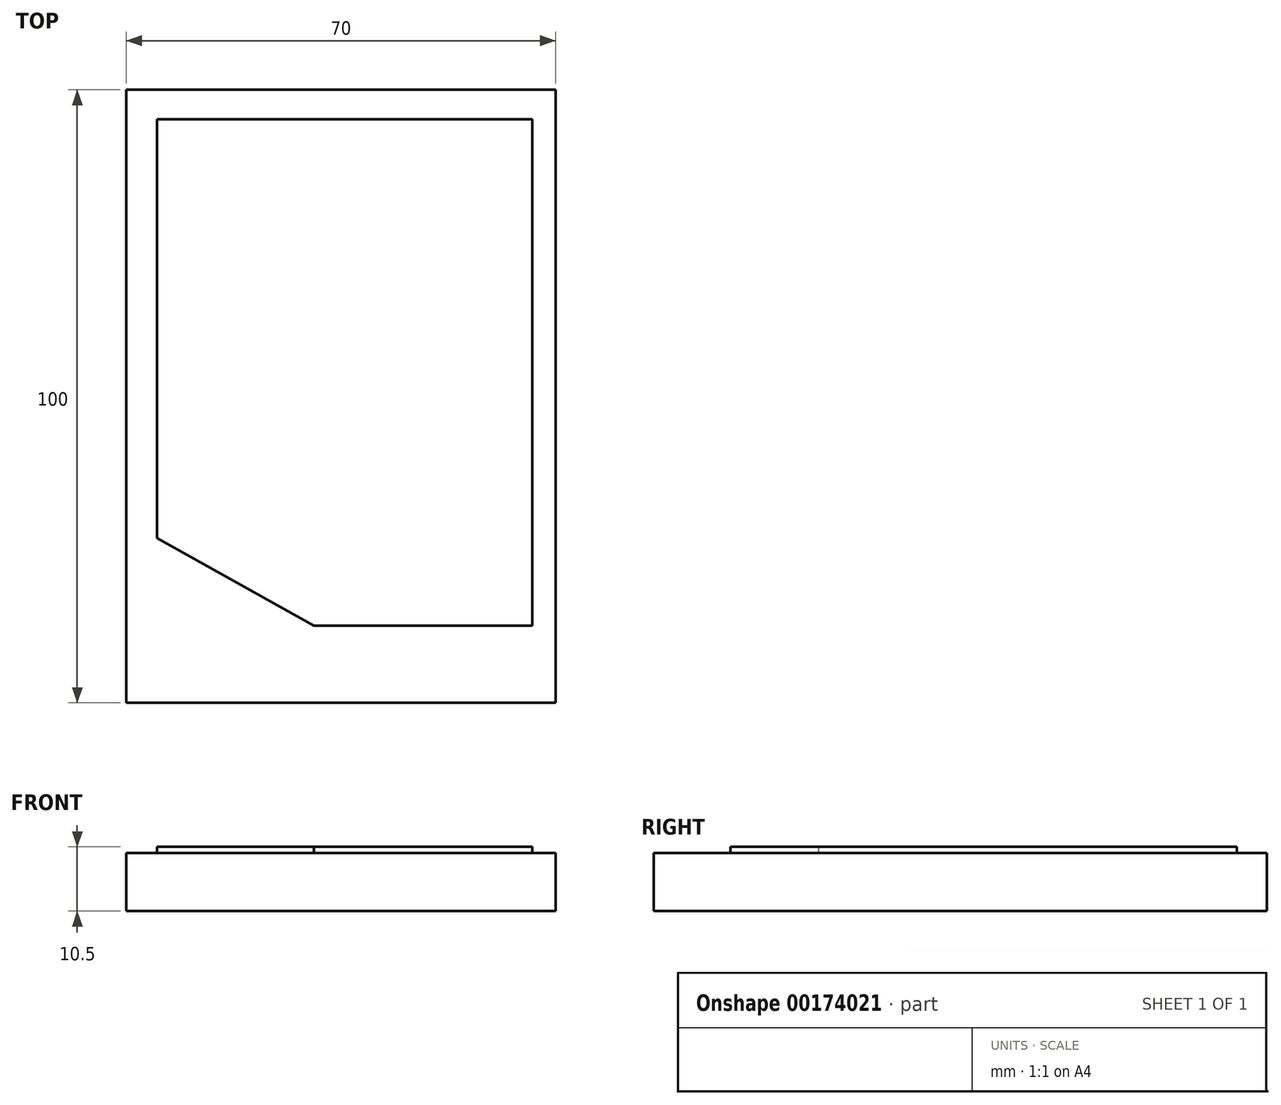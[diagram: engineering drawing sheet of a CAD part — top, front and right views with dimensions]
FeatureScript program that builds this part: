
annotation { "Feature Type Name" : "Feature", "Feature Type Description" : "" }
export const myFeature = defineFeature(function(context is Context, id is Id, definition is map)
    precondition{}
    {
        {
            var Q0;
            Q0=qCreatedBy(makeId("Top.planeOp"),FACE);
            var sketch = newSketch(context, id + "F0", { "sketchPlane" : qUnion([Q0])});
            skLineSegment(sketch, "E0.bottom", {"start": v(35, 50) * mm, "end": v(-35, 50) * mm});
            skLineSegment(sketch, "E0.top", {"start": v(35, -50) * mm, "end": v(-35, -50) * mm});
            skLineSegment(sketch, "E0.left", {"start": v(35, 50) * mm, "end": v(35, -50) * mm});
            skLineSegment(sketch, "E0.right", {"start": v(-35, 50) * mm, "end": v(-35, -50) * mm});
            skPoint(sketch, "E0.middle", {"position": v(0, 0) * mm});
            skSolve(sketch);
        }
        {
            var Q0;
            Q0 = qSketchRegion(id + "F0", true);
            extrude(context, id + "F1", {"entities" : qUnion([Q0]), "depth" : 9.5 * mm});
        }
        {
            var Q0;
            Q0=makeQuery(id+"F1.opExtrude","CAP_FACE",FACE,{"disambiguationData":[OSD([sQuery(id+"F0.wireOp",EDGE,"E0.bottom"),sQuery(id+"F0.wireOp",EDGE,"E0.top"),sQuery(id+"F0.wireOp",EDGE,"E0.left"),sQuery(id+"F0.wireOp",EDGE,"E0.right")])],"isStart":false});
            var sketch = newSketch(context, id + "F2", { "sketchPlane" : qUnion([Q0])});
            skLineSegment(sketch, "E1.bottom", {"start": v(-30, 45.17) * mm, "end": v(31.17, 45.17) * mm});
            skLineSegment(sketch, "E1.top", {"start": v(-4.41, -37.46) * mm, "end": v(31.17, -37.46) * mm});
            skLineSegment(sketch, "E1.left", {"start": v(-30, 45.17) * mm, "end": v(-30, -23.12) * mm});
            skLineSegment(sketch, "E1.right", {"start": v(31.17, 45.17) * mm, "end": v(31.17, -37.46) * mm});
            skLineSegment(sketch, "E2", {"start": v(-30, -23.12) * mm, "end": v(-4.41, -37.46) * mm});
            skSolve(sketch);
        }
        {
            var Q0;
            Q0 = qSketchRegion(id + "F2", true);
            extrude(context, id + "F3", {"entities" : qUnion([Q0]), "operationType" : NewBodyOperationType.ADD, "depth" : 1 * mm});
        }
    });
